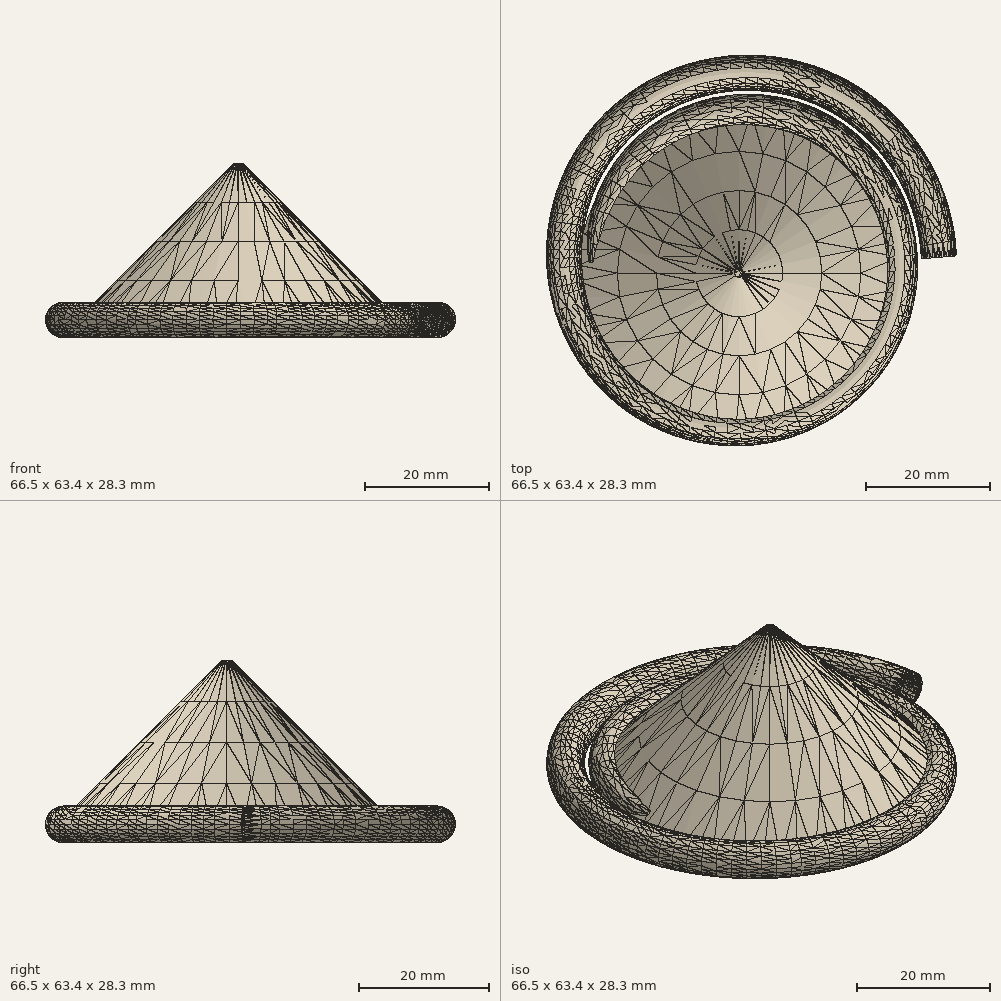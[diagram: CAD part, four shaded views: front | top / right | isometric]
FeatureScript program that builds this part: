
annotation { "Feature Type Name" : "Feature", "Feature Type Description" : "" }
export const myFeature = defineFeature(function(context is Context, id is Id, definition is map)
    precondition{}
    {
        {
            var Q0;
            Q0=qCreatedBy(makeId("Top.planeOp"),FACE);
            var sketch = newSketch(context, id + "F0", { "sketchPlane" : qUnion([Q0])});
            skCircle(sketch, "E0", {"center": v(0, 0) * mm, "radius": 26.1 * mm});
            skSolve(sketch);
        }
        {
            var Q0;
            Q0=makeQuery(id+"F0.imprint","IMPRINT",FACE,{"disambiguationData":[TD([[makeQuery(id+"F0.imprint","IMPRINT",EDGE,{"derivedFrom":sQuery(id+"F0.wireOp",EDGE,"E0")}),1.0]])]});
            extrude(context, id + "F1", {"entities" : qUnion([Q0]), "depth" : 25.4 * mm, "offsetDistance" : 25.4 * mm, "hasDraft" : true, "draftAngle" : 45 * degree, "draftPullDirection" : true});
        }
        {
            var Q0;
            Q0=qCreatedBy(makeId("Top.planeOp"),FACE);
            var sketch = newSketch(context, id + "F2", { "sketchPlane" : qUnion([Q0])});
            skFitSpline(sketch, "E1.0", {"points": [v(26.55, 2.1) * mm, v(26.51, 2.95) * mm, v(26.44, 3.8) * mm, v(26.2, 5.48) * mm, v(26.05, 6.32) * mm, v(25.65, 7.97) * mm, v(25.41, 8.78) * mm, v(24.86, 10.38) * mm, v(24.54, 11.17) * mm, v(23.84, 12.7) * mm, v(23.45, 13.44) * mm, v(22.6, 14.89) * mm, v(22.14, 15.59) * mm, v(21.16, 16.94) * mm, v(20.64, 17.6) * mm, v(19.53, 18.84) * mm, v(18.95, 19.43) * mm, v(17.73, 20.55) * mm, v(17.1, 21.08) * mm, v(15.77, 22.08) * mm, v(15.1, 22.55) * mm, v(13.69, 23.4) * mm, v(12.97, 23.8) * mm, v(11.5, 24.51) * mm, v(10.74, 24.83) * mm, v(9.2, 25.4) * mm, v(8.43, 25.64) * mm, v(6.85, 26.05) * mm, v(6.06, 26.21) * mm, v(4.46, 26.46) * mm, v(3.66, 26.55) * mm, v(2.05, 26.64) * mm, v(1.24, 26.65) * mm, v(-0.37, 26.58) * mm, v(-1.16, 26.5) * mm, v(-2.75, 26.28) * mm, v(-3.53, 26.13) * mm, v(-5.08, 25.76) * mm, v(-5.85, 25.53) * mm, v(-7.34, 25) * mm, v(-8.08, 24.71) * mm, v(-9.51, 24.05) * mm, v(-10.21, 23.68) * mm, v(-11.57, 22.88) * mm, v(-12.22, 22.45) * mm, v(-13.49, 21.52) * mm, v(-14.1, 21.03) * mm, v(-15.26, 19.99) * mm, v(-15.82, 19.44) * mm, v(-16.87, 18.3) * mm, v(-17.36, 17.7) * mm, v(-18.3, 16.46) * mm, v(-18.73, 15.82) * mm, v(-19.53, 14.5) * mm, v(-19.9, 13.83) * mm, v(-20.56, 12.44) * mm, v(-20.86, 11.74) * mm, v(-21.38, 10.3) * mm, v(-21.6, 9.57) * mm, v(-21.98, 8.1) * mm, v(-22.14, 7.35) * mm, v(-22.37, 5.85) * mm, v(-22.44, 5.1) * mm, v(-22.53, 3.6) * mm, v(-22.53, 2.84) * mm, v(-22.46, 1.34) * mm, v(-22.4, 0.6) * mm, v(-22.18, -0.89) * mm, v(-22.04, -1.62) * mm, v(-21.68, -3.07) * mm, v(-21.47, -3.78) * mm, v(-20.98, -5.18) * mm, v(-20.7, -5.87) * mm, v(-20.07, -7.2) * mm, v(-19.73, -7.85) * mm, v(-18.98, -9.12) * mm, v(-18.57, -9.73) * mm, v(-17.7, -10.9) * mm, v(-17.24, -11.48) * mm, v(-16.27, -12.56) * mm, v(-15.75, -13.08) * mm, v(-14.68, -14.05) * mm, v(-14.12, -14.52) * mm, v(-12.97, -15.38) * mm, v(-12.37, -15.78) * mm, v(-11.14, -16.52) * mm, v(-10.5, -16.86) * mm, v(-9.21, -17.48) * mm, v(-8.55, -17.76) * mm, v(-7.21, -18.24) * mm, v(-6.53, -18.45) * mm, v(-5.16, -18.8) * mm, v(-4.46, -18.94) * mm, v(-3.07, -19.15) * mm, v(-2.37, -19.22) * mm, v(-0.96, -19.29) * mm, v(-0.26, -19.29) * mm, v(1.14, -19.22) * mm, v(1.83, -19.16) * mm, v(3.2, -18.95) * mm, v(3.9, -18.82) * mm, v(5.23, -18.48) * mm, v(5.9, -18.28) * mm, v(7.2, -17.82) * mm, v(7.83, -17.56) * mm, v(9.07, -16.97) * mm, v(9.68, -16.65) * mm, v(10.85, -15.95) * mm, v(11.42, -15.57) * mm, v(12.51, -14.76) * mm, v(13.04, -14.33) * mm, v(14.04, -13.42) * mm, v(14.52, -12.94) * mm, v(15.42, -11.94) * mm, v(15.85, -11.42) * mm, v(16.65, -10.35) * mm, v(17.02, -9.79) * mm, v(17.7, -8.65) * mm, v(18.02, -8.06) * mm, v(18.58, -6.86) * mm, v(18.84, -6.24) * mm, v(19.28, -5) * mm, v(19.47, -4.37) * mm, v(19.79, -3.1) * mm, v(19.92, -2.45) * mm, v(20.1, -1.16) * mm, v(20.17, -0.5) * mm, v(20.23, 0.8) * mm, v(20.23, 1.44) * mm, v(20.16, 2.74) * mm, v(20.1, 3.38) * mm, v(19.9, 4.65) * mm, v(19.78, 5.29) * mm, v(19.46, 6.53) * mm, v(19.28, 7.14) * mm, v(18.84, 8.34) * mm, v(18.6, 8.93) * mm, v(18.05, 10.07) * mm, v(17.75, 10.63) * mm, v(17.1, 11.71) * mm, v(16.75, 12.23) * mm, v(16, 13.24) * mm, v(15.6, 13.72) * mm, v(14.75, 14.65) * mm, v(14.3, 15.09) * mm, v(13.38, 15.92) * mm, v(12.9, 16.3) * mm, v(11.9, 17.04) * mm, v(11.4, 17.38) * mm, v(10.33, 18) * mm, v(9.8, 18.3) * mm, v(8.68, 18.81) * mm, v(8.12, 19.04) * mm, v(6.97, 19.45) * mm, v(6.39, 19.62) * mm, v(5.21, 19.9) * mm, v(4.62, 20.02) * mm, v(3.42, 20.2) * mm, v(2.83, 20.25) * mm, v(1.63, 20.3) * mm, v(1.03, 20.3) * mm, v(-0.16, 20.23) * mm, v(-0.75, 20.17) * mm, v(-1.92, 19.98) * mm, v(-2.5, 19.87) * mm, v(-3.64, 19.57) * mm, v(-4.2, 19.4) * mm, v(-5.3, 19) * mm, v(-5.84, 18.77) * mm, v(-6.89, 18.26) * mm, v(-7.4, 17.98) * mm, v(-8.39, 17.38) * mm, v(-8.87, 17.05) * mm, v(-9.79, 16.36) * mm, v(-10.23, 15.99) * mm, v(-11.07, 15.21) * mm, v(-11.47, 14.8) * mm, v(-12.23, 13.95) * mm, v(-12.59, 13.5) * mm, v(-13.25, 12.6) * mm, v(-13.56, 12.12) * mm, v(-14.13, 11.15) * mm, v(-14.4, 10.65) * mm, v(-14.86, 9.63) * mm, v(-15.07, 9.11) * mm, v(-15.43, 8.06) * mm, v(-15.59, 7.53) * mm, v(-15.85, 6.45) * mm, v(-15.95, 5.9) * mm, v(-16.1, 4.82) * mm, v(-16.15, 4.27) * mm, v(-16.19, 3.18) * mm, v(-16.18, 2.63) * mm, v(-16.11, 1.55) * mm, v(-16.05, 1) * mm, v(-15.88, -0.06) * mm, v(-15.77, -0.59) * mm, v(-15.5, -1.63) * mm, v(-15.33, -2.14) * mm, v(-14.96, -3.14) * mm, v(-14.75, -3.63) * mm, v(-14.28, -4.58) * mm, v(-14.03, -5.04) * mm, v(-13.47, -5.94) * mm, v(-13.18, -6.38) * mm, v(-12.54, -7.2) * mm, v(-12.2, -7.6) * mm, v(-11.5, -8.37) * mm, v(-11.12, -8.73) * mm, v(-10.34, -9.42) * mm, v(-9.94, -9.74) * mm, v(-9.1, -10.34) * mm, v(-8.67, -10.62) * mm, v(-7.78, -11.13) * mm, v(-7.33, -11.36) * mm, v(-6.4, -11.78) * mm, v(-5.93, -11.97) * mm, v(-4.98, -12.3) * mm, v(-4.5, -12.43) * mm, v(-3.51, -12.66) * mm, v(-3.02, -12.75) * mm, v(-2.03, -12.88) * mm, v(-1.54, -12.92) * mm, v(-0.55, -12.95) * mm, v(-0.05, -12.94) * mm, v(0.93, -12.87) * mm, v(1.42, -12.82) * mm, v(2.38, -12.65) * mm, v(2.86, -12.55) * mm, v(3.8, -12.3) * mm, v(4.25, -12.15) * mm, v(5.15, -11.8) * mm, v(5.6, -11.61) * mm, v(6.45, -11.18) * mm, v(6.87, -10.95) * mm, v(7.68, -10.44) * mm, v(8.06, -10.17) * mm, v(8.81, -9.6) * mm, v(9.17, -9.29) * mm, v(9.85, -8.64) * mm, v(10.17, -8.3) * mm, v(10.78, -7.6) * mm, v(11.07, -7.23) * mm, v(11.6, -6.48) * mm, v(11.85, -6.09) * mm, v(12.3, -5.3) * mm, v(12.51, -4.88) * mm, v(12.89, -4.05) * mm, v(13.05, -3.62) * mm, v(13.33, -2.76) * mm, v(13.45, -2.33) * mm, v(13.65, -1.45) * mm, v(13.73, -1) * mm, v(13.84, -0.12) * mm, v(13.87, 0.32) * mm, v(13.9, 1.2) * mm, v(13.88, 1.65) * mm, v(13.81, 2.53) * mm, v(13.76, 2.96) * mm, v(13.6, 3.83) * mm, v(13.51, 4.25) * mm, v(13.28, 5.09) * mm, v(13.14, 5.5) * mm, v(12.83, 6.3) * mm, v(12.65, 6.69) * mm, v(12.26, 7.45) * mm, v(12.05, 7.82) * mm, v(11.6, 8.53) * mm, v(11.35, 8.88) * mm, v(10.83, 9.54) * mm, v(10.55, 9.86) * mm, v(9.98, 10.46) * mm, v(9.67, 10.74) * mm, v(9.04, 11.28) * mm, v(8.71, 11.53) * mm, v(8.04, 12) * mm, v(7.7, 12.22) * mm, v(6.98, 12.61) * mm, v(6.61, 12.8) * mm, v(5.87, 13.11) * mm, v(5.5, 13.26) * mm, v(4.73, 13.5) * mm, v(4.34, 13.6) * mm, v(3.57, 13.77) * mm, v(3.17, 13.84) * mm, v(2.39, 13.92) * mm, v(2, 13.95) * mm, v(1.21, 13.96) * mm, v(0.82, 13.95) * mm, v(0.05, 13.88) * mm, v(-0.33, 13.83) * mm, v(-1.1, 13.69) * mm, v(-1.46, 13.6) * mm, v(-2.2, 13.38) * mm, v(-2.56, 13.26) * mm, v(-3.26, 12.98) * mm, v(-3.6, 12.82) * mm, v(-4.27, 12.47) * mm, v(-4.6, 12.28) * mm, v(-5.21, 11.87) * mm, v(-5.51, 11.66) * mm, v(-6.09, 11.2) * mm, v(-6.36, 10.95) * mm, v(-6.88, 10.44) * mm, v(-7.13, 10.17) * mm, v(-7.6, 9.6) * mm, v(-7.8, 9.32) * mm, v(-8.21, 8.73) * mm, v(-8.4, 8.42) * mm, v(-8.74, 7.8) * mm, v(-8.89, 7.47) * mm, v(-9.16, 6.82) * mm, v(-9.28, 6.5) * mm, v(-9.49, 5.82) * mm, v(-9.57, 5.49) * mm, v(-9.7, 4.8) * mm, v(-9.76, 4.47) * mm, v(-9.83, 3.78) * mm, v(-9.85, 3.44) * mm, v(-9.85, 2.76) * mm, v(-9.83, 2.43) * mm, v(-9.76, 1.76) * mm, v(-9.71, 1.42) * mm, v(-9.58, 0.77) * mm, v(-9.5, 0.45) * mm, v(-9.3, -0.18) * mm, v(-9.09, -0.8) * mm, v(-8.8, -1.39) * mm, v(-8.5, -1.96) * mm, v(-8.33, -2.23) * mm, v(-7.97, -2.77) * mm, v(-7.78, -3.02) * mm, v(-7.37, -3.5) * mm, v(-7.16, -3.74) * mm, v(-6.71, -4.18) * mm, v(-6.48, -4.39) * mm, v(-6, -4.78) * mm, v(-5.75, -4.96) * mm, v(-5.23, -5.3) * mm, v(-4.97, -5.45) * mm, v(-4.43, -5.73) * mm, v(-4.15, -5.86) * mm, v(-3.6, -6.08) * mm, v(-3.3, -6.18) * mm, v(-2.74, -6.35) * mm, v(-2.45, -6.41) * mm, v(-1.87, -6.52) * mm, v(-1.58, -6.56) * mm, v(-1, -6.6) * mm, v(-0.7, -6.62) * mm, v(-0.13, -6.6) * mm, v(0.15, -6.59) * mm, v(0.72, -6.52) * mm, v(1.28, -6.43) * mm, v(2.1, -6.2) * mm, v(2.87, -5.91) * mm, v(3.6, -5.54) * mm, v(4.06, -5.25) * mm, v(4.5, -4.94) * mm, v(4.7, -4.78) * mm, v(5.11, -4.43) * mm, v(5.3, -4.25) * mm, v(5.66, -3.87) * mm, v(5.83, -3.67) * mm, v(6.15, -3.26) * mm, v(6.3, -3.05) * mm, v(6.57, -2.61) * mm, v(6.69, -2.39) * mm, v(6.91, -1.94) * mm, v(7.01, -1.7) * mm, v(7.19, -1.24) * mm, v(7.26, -1) * mm, v(7.39, -0.52) * mm, v(7.44, -0.28) * mm, v(7.51, 0.2) * mm, v(7.57, 0.68) * mm, v(7.57, 1.4) * mm, v(7.5, 2.1) * mm, v(7.37, 2.78) * mm, v(7.18, 3.43) * mm, v(6.92, 4.06) * mm, v(6.6, 4.65) * mm, v(6.23, 5.2) * mm, v(5.82, 5.7) * mm, v(5.36, 6.14) * mm, v(4.87, 6.53) * mm, v(4.35, 6.87) * mm, v(3.81, 7.14) * mm, v(3.25, 7.36) * mm, v(2.68, 7.52) * mm, v(2.11, 7.62) * mm, v(1.54, 7.66) * mm, v(0.98, 7.64) * mm, v(0.43, 7.57) * mm, v(-0.1, 7.45) * mm, v(-0.6, 7.27) * mm, v(-1.07, 7.05) * mm, v(-1.51, 6.79) * mm, v(-1.92, 6.48) * mm, v(-2.28, 6.15) * mm, v(-2.6, 5.79) * mm, v(-2.88, 5.4) * mm, v(-3.1, 5) * mm, v(-3.3, 4.58) * mm, v(-3.43, 4.16) * mm, v(-3.53, 3.73) * mm, v(-3.57, 3.3) * mm, v(-3.57, 2.89) * mm, v(-3.53, 2.48) * mm, v(-3.45, 2.09) * mm, v(-3.34, 1.72) * mm, v(-3.18, 1.37) * mm, v(-3, 1.04) * mm, v(-2.79, 0.75) * mm, v(-2.55, 0.49) * mm, v(-2.3, 0.26) * mm, v(-2.03, 0.06) * mm, v(-1.75, -0.1) * mm, v(-1.46, -0.23) * mm, v(-1.17, -0.32) * mm, v(-0.88, -0.38) * mm, v(-0.6, -0.4) * mm, v(-0.31, -0.4) * mm, v(-0.05, -0.36) * mm, v(0.2, -0.3) * mm, v(0.44, -0.2) * mm, v(0.66, -0.1) * mm, v(0.85, 0.03) * mm, v(1.02, 0.18) * mm, v(1.17, 0.33) * mm, v(1.29, 0.5) * mm, v(1.39, 0.68) * mm, v(1.46, 0.85) * mm, v(1.5, 1.03) * mm, v(1.53, 1.2) * mm, v(1.52, 1.37) * mm, v(1.5, 1.52) * mm, v(1.46, 1.67) * mm, v(1.4, 1.8) * mm, v(1.33, 1.92) * mm, v(1.24, 2.01) * mm, v(1.18, 2.07) * mm, v(1.15, 2.1) * mm]});
            skSolve(sketch);
        }
        {
            var Q0;
            Q0=qCreatedBy(makeId("Front.planeOp"),FACE);
            var sketch = newSketch(context, id + "F3", { "sketchPlane" : qUnion([Q0])});
            skCircle(sketch, "E2", {"center": v(26.06, 0) * mm, "radius": 2.86 * mm});
            skSolve(sketch);
        }
        {
            var Q0;
            Q0=makeQuery(id+"F3.imprint","IMPRINT",FACE,{"disambiguationData":[TD([[makeQuery(id+"F3.imprint","IMPRINT",EDGE,{"derivedFrom":sQuery(id+"F3.wireOp",EDGE,"E2")}),1.0]])]});
            var Q1;
            Q1=qConstructionFilter(qBodyType(qCreatedBy(id+"F2",EDGE),BodyType.WIRE),ConstructionObject.NO);
            sweep(context, id + "F4", {"profiles" : qUnion([Q0]), "path" : qUnion([Q1])});
        }
        {
            var Q0;
            Q0=makeQuery(id+"F4.opSweep","CAP_FACE",FACE,{"disambiguationData":[OSD([sQuery(id+"F2.wireOp",VERTEX,"E1.0.end"),sQuery(id+"F3.wireOp",EDGE,"E2")])],"isStart":true});
            var Q1;
            Q1=makeQuery(id+"F4.opSweep","CAP_FACE",FACE,{"disambiguationData":[OSD([sQuery(id+"F2.wireOp",VERTEX,"E1.0.start"),sQuery(id+"F3.wireOp",EDGE,"E2")])],"isStart":false});
            var Q2;
            Q2=makeQuery(id+"F4.opSweep","SWEPT_BODY",BODY,{"disambiguationData":[OSD([sQuery(id+"F2.wireOp",EDGE,"E1.0"),sQuery(id+"F3.wireOp",EDGE,"E2")])]});
            shell(context, id + "F5", {"entities" : qUnion([Q0, Q1]), "parts" : qUnion([Q2]), "thickness" : 0.5 * mm});
        }
    });
